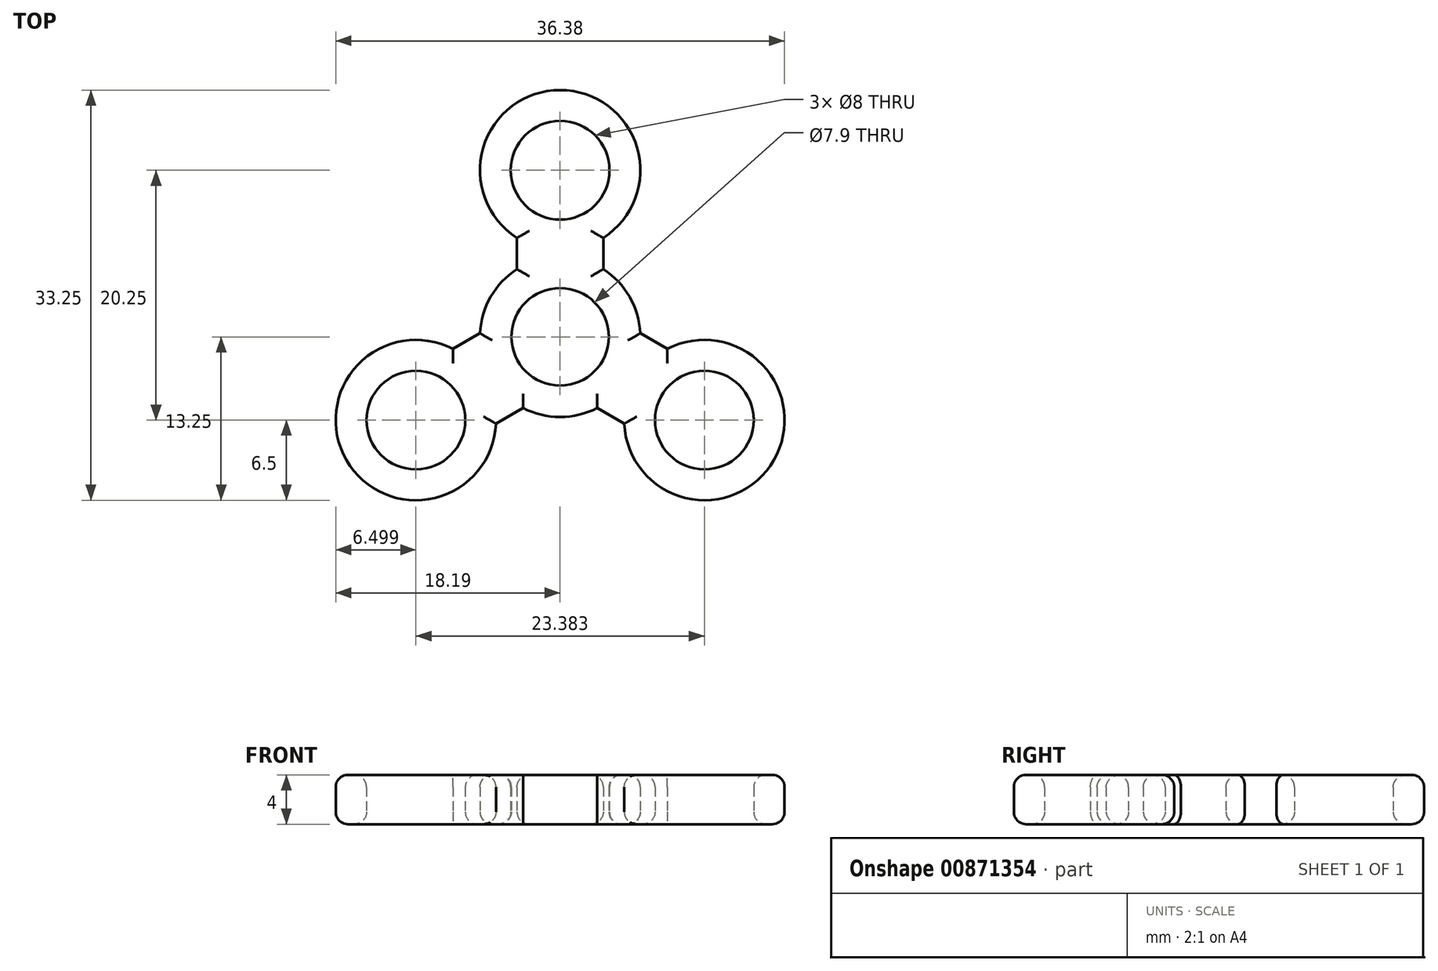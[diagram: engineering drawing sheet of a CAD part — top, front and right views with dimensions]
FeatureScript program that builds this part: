
annotation { "Feature Type Name" : "Feature", "Feature Type Description" : "" }
export const myFeature = defineFeature(function(context is Context, id is Id, definition is map)
    precondition{}
    {
        {
            var Q0;
            Q0=qCreatedBy(makeId("Top.planeOp"),FACE);
            var sketch = newSketch(context, id + "F0", { "sketchPlane" : qUnion([Q0])});
            skCircle(sketch, "E0", {"center": v(0, 0) * mm, "radius": 20 * mm});
            skCircle(sketch, "E1", {"center": v(0, 0) * mm, "radius": 3.95 * mm});
            skLineSegment(sketch, "E2", {"start": v(0, 0) * mm, "end": v(0, 20) * mm, "construction": true});
            skCircle(sketch, "E3", {"center": v(0, 13.5) * mm, "radius": 4 * mm});
            skCircle(sketch, "E4", {"center": v(0, 13.5) * mm, "radius": 6.5 * mm});
            skCircle(sketch, "E5", {"center": v(0, 0) * mm, "radius": 6.5 * mm});
            skLineSegment(sketch, "E6", {"start": v(-3.5, 5.48) * mm, "end": v(-3.5, 8.02) * mm});
            skLineSegment(sketch, "E7", {"start": v(3.5, 5.48) * mm, "end": v(3.5, 8.02) * mm});
            skCircle(sketch, "E8.1.0", {"center": v(-11.7, -6.75) * mm, "radius": 4 * mm});
            skLineSegment(sketch, "E8.1.1", {"start": v(0, 0) * mm, "end": v(-17.32, -10) * mm, "construction": true});
            skLineSegment(sketch, "E8.1.2", {"start": v(-3, -5.77) * mm, "end": v(-5.2, -7.04) * mm});
            skLineSegment(sketch, "E8.1.3", {"start": v(-6.5, 0.3) * mm, "end": v(-8.7, -0.98) * mm});
            skCircle(sketch, "E8.1.4", {"center": v(-11.7, -6.75) * mm, "radius": 6.5 * mm});
            skCircle(sketch, "E8.2.0", {"center": v(11.7, -6.75) * mm, "radius": 4 * mm});
            skLineSegment(sketch, "E8.2.1", {"start": v(0, 0) * mm, "end": v(17.32, -10) * mm, "construction": true});
            skLineSegment(sketch, "E8.2.2", {"start": v(6.5, 0.3) * mm, "end": v(8.7, -0.98) * mm});
            skLineSegment(sketch, "E8.2.3", {"start": v(3, -5.77) * mm, "end": v(5.2, -7.04) * mm});
            skCircle(sketch, "E8.2.4", {"center": v(11.7, -6.75) * mm, "radius": 6.5 * mm});
            skSolve(sketch);
        }
        {
            var Q0;
            Q0=makeQuery(id+"F0.imprint","IMPRINT",FACE,{"disambiguationData":[TD([[makeQuery(id+"F0.imprint","IMPRINT",EDGE,{"derivedFrom":sQuery(id+"F0.wireOp",EDGE,"E8.1.0")}),-1.0]])]});
            var Q1;
            Q1=makeQuery(id+"F0.imprint","IMPRINT",FACE,{"disambiguationData":[TD([[makeQuery(id+"F0.imprint","IMPRINT",EDGE,{"derivedFrom":sQuery(id+"F0.wireOp",EDGE,"E8.2.0")}),-1.0]])]});
            var Q2;
            {var subQ0=sQuery(id+"F0.wireOp",EDGE,"E6");Q2=makeQuery(id+"F0.imprint","IMPRINT",FACE,{"disambiguationData":[TD([[makeQuery(id+"F0.imprint","IMPRINT",EDGE,{"derivedFrom":subQ0}),-1.0]])]});}
            var Q3;
            Q3=makeQuery(id+"F0.imprint","IMPRINT",FACE,{"disambiguationData":[TD([[makeQuery(id+"F0.imprint","IMPRINT",EDGE,{"derivedFrom":sQuery(id+"F0.wireOp",EDGE,"E1")}),-1.0]])]});
            var Q4;
            Q4=makeQuery(id+"F0.imprint","IMPRINT",FACE,{"disambiguationData":[TD([[makeQuery(id+"F0.imprint","IMPRINT",EDGE,{"derivedFrom":sQuery(id+"F0.wireOp",EDGE,"E3")}),-1.0]])]});
            var Q5;
            {var subQ0=sQuery(id+"F0.wireOp",EDGE,"E8.1.2");Q5=makeQuery(id+"F0.imprint","IMPRINT",FACE,{"disambiguationData":[TD([[makeQuery(id+"F0.imprint","IMPRINT",EDGE,{"derivedFrom":subQ0}),-1.0]])]});}
            var Q6;
            {var subQ0=sQuery(id+"F0.wireOp",EDGE,"E8.2.2");Q6=makeQuery(id+"F0.imprint","IMPRINT",FACE,{"disambiguationData":[TD([[makeQuery(id+"F0.imprint","IMPRINT",EDGE,{"derivedFrom":subQ0}),-1.0]])]});}
            extrude(context, id + "F1", {"entities" : qUnion([Q0, Q1, Q2, Q3, Q4, Q5, Q6]), "depth" : 4 * mm, "offsetDistance" : 25 * mm});
        }
        {
            var Q0;
            Q0=makeQuery(id+"F1.opExtrude","CAP_FACE",FACE,{"disambiguationData":[OSD([sQuery(id+"F0.wireOp",EDGE,"E1"),sQuery(id+"F0.wireOp",EDGE,"E3"),sQuery(id+"F0.wireOp",EDGE,"E4"),sQuery(id+"F0.wireOp",EDGE,"E5"),sQuery(id+"F0.wireOp",EDGE,"E6"),sQuery(id+"F0.wireOp",EDGE,"E7"),sQuery(id+"F0.wireOp",EDGE,"E8.1.0"),sQuery(id+"F0.wireOp",EDGE,"E8.1.2"),sQuery(id+"F0.wireOp",EDGE,"E8.1.3"),sQuery(id+"F0.wireOp",EDGE,"E8.1.4"),sQuery(id+"F0.wireOp",EDGE,"E8.2.0"),sQuery(id+"F0.wireOp",EDGE,"E8.2.2"),sQuery(id+"F0.wireOp",EDGE,"E8.2.3"),sQuery(id+"F0.wireOp",EDGE,"E8.2.4")])],"isStart":false});
            var Q1;
            Q1=makeQuery(id+"F1.opExtrude","CAP_EDGE",EDGE,{"disambiguationData":[OSD([sQuery(id+"F0.wireOp",EDGE,"E8.1.2")])],"isStart":true});
            var Q2;
            Q2=makeQuery(id+"F1.opExtrude","CAP_FACE",FACE,{"disambiguationData":[OSD([sQuery(id+"F0.wireOp",EDGE,"E1"),sQuery(id+"F0.wireOp",EDGE,"E3"),sQuery(id+"F0.wireOp",EDGE,"E4"),sQuery(id+"F0.wireOp",EDGE,"E5"),sQuery(id+"F0.wireOp",EDGE,"E6"),sQuery(id+"F0.wireOp",EDGE,"E7"),sQuery(id+"F0.wireOp",EDGE,"E8.1.0"),sQuery(id+"F0.wireOp",EDGE,"E8.1.2"),sQuery(id+"F0.wireOp",EDGE,"E8.1.3"),sQuery(id+"F0.wireOp",EDGE,"E8.1.4"),sQuery(id+"F0.wireOp",EDGE,"E8.2.0"),sQuery(id+"F0.wireOp",EDGE,"E8.2.2"),sQuery(id+"F0.wireOp",EDGE,"E8.2.3"),sQuery(id+"F0.wireOp",EDGE,"E8.2.4")])],"isStart":true});
            fillet(context, id + "F2", {"entities" : qUnion([Q0, Q1, Q2]), "radius" : 1 * mm, "tangentPropagation" : true, "allowEdgeOverflow" : false});
        }
    });
